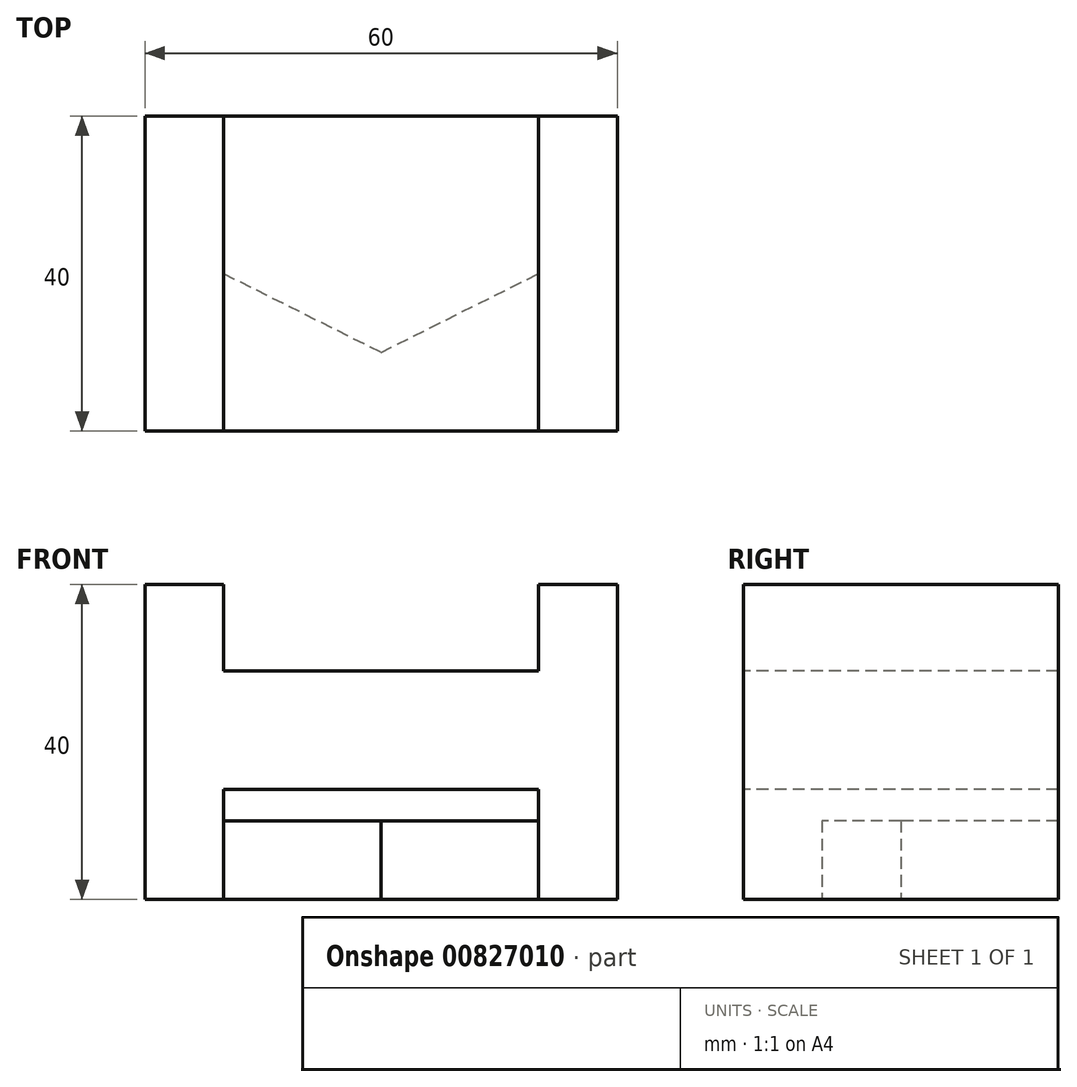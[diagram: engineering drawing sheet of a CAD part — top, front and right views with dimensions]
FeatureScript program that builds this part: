
annotation { "Feature Type Name" : "Feature", "Feature Type Description" : "" }
export const myFeature = defineFeature(function(context is Context, id is Id, definition is map)
    precondition{}
    {
        {
            var Q0;
            Q0=qCreatedBy(makeId("Top.planeOp"),FACE);
            var sketch = newSketch(context, id + "F0", { "sketchPlane" : qUnion([Q0])});
            skLineSegment(sketch, "E0.bottom", {"start": v(0, 0) * mm, "end": v(60, 0) * mm});
            skLineSegment(sketch, "E0.top", {"start": v(0, 40) * mm, "end": v(60, 40) * mm});
            skLineSegment(sketch, "E0.left", {"start": v(0, 0) * mm, "end": v(0, 40) * mm});
            skLineSegment(sketch, "E0.right", {"start": v(60, 0) * mm, "end": v(60, 40) * mm});
            skLineSegment(sketch, "E1", {"start": v(10, 40) * mm, "end": v(10, 0) * mm});
            skLineSegment(sketch, "E2", {"start": v(50, 40) * mm, "end": v(50, 0) * mm});
            skLineSegment(sketch, "E3", {"start": v(10, 20) * mm, "end": v(50, 20) * mm});
            skLineSegment(sketch, "E4", {"start": v(30, 40) * mm, "end": v(30, 0) * mm});
            skLineSegment(sketch, "E5", {"start": v(10, 10) * mm, "end": v(50, 10) * mm});
            skLineSegment(sketch, "E6", {"start": v(10, 30) * mm, "end": v(50, 30) * mm});
            skLineSegment(sketch, "E7", {"start": v(10, 20) * mm, "end": v(30, 10) * mm});
            skLineSegment(sketch, "E8", {"start": v(30, 10) * mm, "end": v(50, 20) * mm});
            skSolve(sketch);
        }
        {
            var Q0;
            {var subQ0=sQuery(id+"F0.wireOp",EDGE,"E1");var subQ1=sQuery(id+"F0.wireOp",EDGE,"E0.top");var subQ2=makeQuery(id+"F0.imprint","INTERSECT",VERTEX,{"derivedFrom":[subQ1,subQ0]});Q0=makeQuery(id+"F0.imprint","IMPRINT",FACE,{"disambiguationData":[TD([[makeQuery(id+"F0.imprint","IMPRINT",EDGE,{"disambiguationData":[TD([[subQ2,-1.0]])],"derivedFrom":subQ1}),-1.0]])]});}
            var Q1;
            {var subQ0=sQuery(id+"F0.wireOp",EDGE,"E2");var subQ1=sQuery(id+"F0.wireOp",EDGE,"E0.top");var subQ2=makeQuery(id+"F0.imprint","INTERSECT",VERTEX,{"derivedFrom":[subQ1,subQ0]});Q1=makeQuery(id+"F0.imprint","IMPRINT",FACE,{"disambiguationData":[TD([[makeQuery(id+"F0.imprint","IMPRINT",EDGE,{"disambiguationData":[TD([[subQ2,1.0]])],"derivedFrom":subQ1}),-1.0]])]});}
            var Q2;
            {var subQ0=sQuery(id+"F0.wireOp",EDGE,"E3");var subQ5=sQuery(id+"F0.wireOp",EDGE,"E4");var subQ6=makeQuery(id+"F0.imprint","INTERSECT",VERTEX,{"derivedFrom":[subQ0,subQ5]});Q2=makeQuery(id+"F0.imprint","IMPRINT",FACE,{"disambiguationData":[TD([[makeQuery(id+"F0.imprint","IMPRINT",EDGE,{"disambiguationData":[TD([[subQ6,1.0]])],"derivedFrom":subQ5}),1.0]])]});}
            var Q3;
            {var subQ0=sQuery(id+"F0.wireOp",EDGE,"E3");var subQ5=sQuery(id+"F0.wireOp",EDGE,"E4");var subQ6=makeQuery(id+"F0.imprint","INTERSECT",VERTEX,{"derivedFrom":[subQ0,subQ5]});Q3=makeQuery(id+"F0.imprint","IMPRINT",FACE,{"disambiguationData":[TD([[makeQuery(id+"F0.imprint","IMPRINT",EDGE,{"disambiguationData":[TD([[subQ6,1.0]])],"derivedFrom":subQ5}),-1.0]])]});}
            var Q4;
            {var subQ0=sQuery(id+"F0.wireOp",EDGE,"E7");Q4=makeQuery(id+"F0.imprint","IMPRINT",FACE,{"disambiguationData":[TD([[makeQuery(id+"F0.imprint","IMPRINT",EDGE,{"derivedFrom":subQ0}),1.0]])]});}
            var Q5;
            {var subQ0=sQuery(id+"F0.wireOp",EDGE,"E8");Q5=makeQuery(id+"F0.imprint","IMPRINT",FACE,{"disambiguationData":[TD([[makeQuery(id+"F0.imprint","IMPRINT",EDGE,{"derivedFrom":subQ0}),1.0]])]});}
            extrude(context, id + "F1", {"entities" : qUnion([Q0, Q1, Q2, Q3, Q4, Q5]), "depth" : 10 * mm, "offsetDistance" : 25 * mm});
        }
        {
            var Q0;
            {var subQ0=sQuery(id+"F0.wireOp",EDGE,"E0.left");Q0=makeQuery(id+"F0.imprint","IMPRINT",FACE,{"disambiguationData":[TD([[makeQuery(id+"F0.imprint","IMPRINT",EDGE,{"derivedFrom":subQ0}),-1.0]])]});}
            var Q1;
            {var subQ4=sQuery(id+"F0.wireOp",EDGE,"E0.right");Q1=makeQuery(id+"F0.imprint","IMPRINT",FACE,{"disambiguationData":[TD([[makeQuery(id+"F0.imprint","IMPRINT",EDGE,{"derivedFrom":subQ4}),1.0]])]});}
            extrude(context, id + "F2", {"entities" : qUnion([Q0, Q1]), "operationType" : NewBodyOperationType.ADD, "depth" : 40 * mm, "offsetDistance" : 25 * mm});
        }
        {
            var Q0;
            {var subQ0=sQuery(id+"F0.wireOp",EDGE,"E2");var subQ1=sQuery(id+"F0.wireOp",EDGE,"E0.top");var subQ2=makeQuery(id+"F0.imprint","INTERSECT",VERTEX,{"derivedFrom":[subQ1,subQ0]});Q0=makeQuery(id+"F0.imprint","IMPRINT",FACE,{"disambiguationData":[TD([[makeQuery(id+"F0.imprint","IMPRINT",EDGE,{"disambiguationData":[TD([[subQ2,1.0]])],"derivedFrom":subQ1}),-1.0]])]});}
            var Q1;
            {var subQ0=sQuery(id+"F0.wireOp",EDGE,"E1");var subQ1=sQuery(id+"F0.wireOp",EDGE,"E0.top");var subQ2=makeQuery(id+"F0.imprint","INTERSECT",VERTEX,{"derivedFrom":[subQ1,subQ0]});Q1=makeQuery(id+"F0.imprint","IMPRINT",FACE,{"disambiguationData":[TD([[makeQuery(id+"F0.imprint","IMPRINT",EDGE,{"disambiguationData":[TD([[subQ2,-1.0]])],"derivedFrom":subQ1}),-1.0]])]});}
            var Q2;
            {var subQ0=sQuery(id+"F0.wireOp",EDGE,"E3");var subQ5=sQuery(id+"F0.wireOp",EDGE,"E4");var subQ6=makeQuery(id+"F0.imprint","INTERSECT",VERTEX,{"derivedFrom":[subQ0,subQ5]});Q2=makeQuery(id+"F0.imprint","IMPRINT",FACE,{"disambiguationData":[TD([[makeQuery(id+"F0.imprint","IMPRINT",EDGE,{"disambiguationData":[TD([[subQ6,1.0]])],"derivedFrom":subQ5}),-1.0]])]});}
            var Q3;
            {var subQ0=sQuery(id+"F0.wireOp",EDGE,"E3");var subQ5=sQuery(id+"F0.wireOp",EDGE,"E4");var subQ6=makeQuery(id+"F0.imprint","INTERSECT",VERTEX,{"derivedFrom":[subQ0,subQ5]});Q3=makeQuery(id+"F0.imprint","IMPRINT",FACE,{"disambiguationData":[TD([[makeQuery(id+"F0.imprint","IMPRINT",EDGE,{"disambiguationData":[TD([[subQ6,1.0]])],"derivedFrom":subQ5}),1.0]])]});}
            var Q4;
            {var subQ0=sQuery(id+"F0.wireOp",EDGE,"E7");Q4=makeQuery(id+"F0.imprint","IMPRINT",FACE,{"disambiguationData":[TD([[makeQuery(id+"F0.imprint","IMPRINT",EDGE,{"derivedFrom":subQ0}),1.0]])]});}
            var Q5;
            {var subQ0=sQuery(id+"F0.wireOp",EDGE,"E8");Q5=makeQuery(id+"F0.imprint","IMPRINT",FACE,{"disambiguationData":[TD([[makeQuery(id+"F0.imprint","IMPRINT",EDGE,{"derivedFrom":subQ0}),1.0]])]});}
            var Q6;
            {var subQ0=sQuery(id+"F0.wireOp",EDGE,"E2");var subQ1=sQuery(id+"F0.wireOp",EDGE,"E0.bottom");var subQ2=makeQuery(id+"F0.imprint","INTERSECT",VERTEX,{"derivedFrom":[subQ1,subQ0]});Q6=makeQuery(id+"F0.imprint","IMPRINT",FACE,{"disambiguationData":[TD([[makeQuery(id+"F0.imprint","IMPRINT",EDGE,{"disambiguationData":[TD([[subQ2,1.0]])],"derivedFrom":subQ1}),1.0]])]});}
            var Q7;
            {var subQ0=sQuery(id+"F0.wireOp",EDGE,"E1");var subQ1=sQuery(id+"F0.wireOp",EDGE,"E0.bottom");var subQ2=makeQuery(id+"F0.imprint","INTERSECT",VERTEX,{"derivedFrom":[subQ1,subQ0]});Q7=makeQuery(id+"F0.imprint","IMPRINT",FACE,{"disambiguationData":[TD([[makeQuery(id+"F0.imprint","IMPRINT",EDGE,{"disambiguationData":[TD([[subQ2,-1.0]])],"derivedFrom":subQ1}),1.0]])]});}
            var Q8;
            {var subQ0=sQuery(id+"F0.wireOp",EDGE,"E7");Q8=makeQuery(id+"F0.imprint","IMPRINT",FACE,{"disambiguationData":[TD([[makeQuery(id+"F0.imprint","IMPRINT",EDGE,{"derivedFrom":subQ0}),-1.0]])]});}
            var Q9;
            {var subQ0=sQuery(id+"F0.wireOp",EDGE,"E8");Q9=makeQuery(id+"F0.imprint","IMPRINT",FACE,{"disambiguationData":[TD([[makeQuery(id+"F0.imprint","IMPRINT",EDGE,{"derivedFrom":subQ0}),-1.0]])]});}
            extrude(context, id + "F3", {"entities" : qUnion([Q0, Q1, Q2, Q3, Q4, Q5, Q6, Q7, Q8, Q9]), "operationType" : NewBodyOperationType.ADD, "depth" : 29 * mm, "offsetDistance" : 25 * mm, "hasSecondDirection" : true, "secondDirectionOppositeDirection" : false, "secondDirectionDepth" : 14 * mm});
        }
    });
